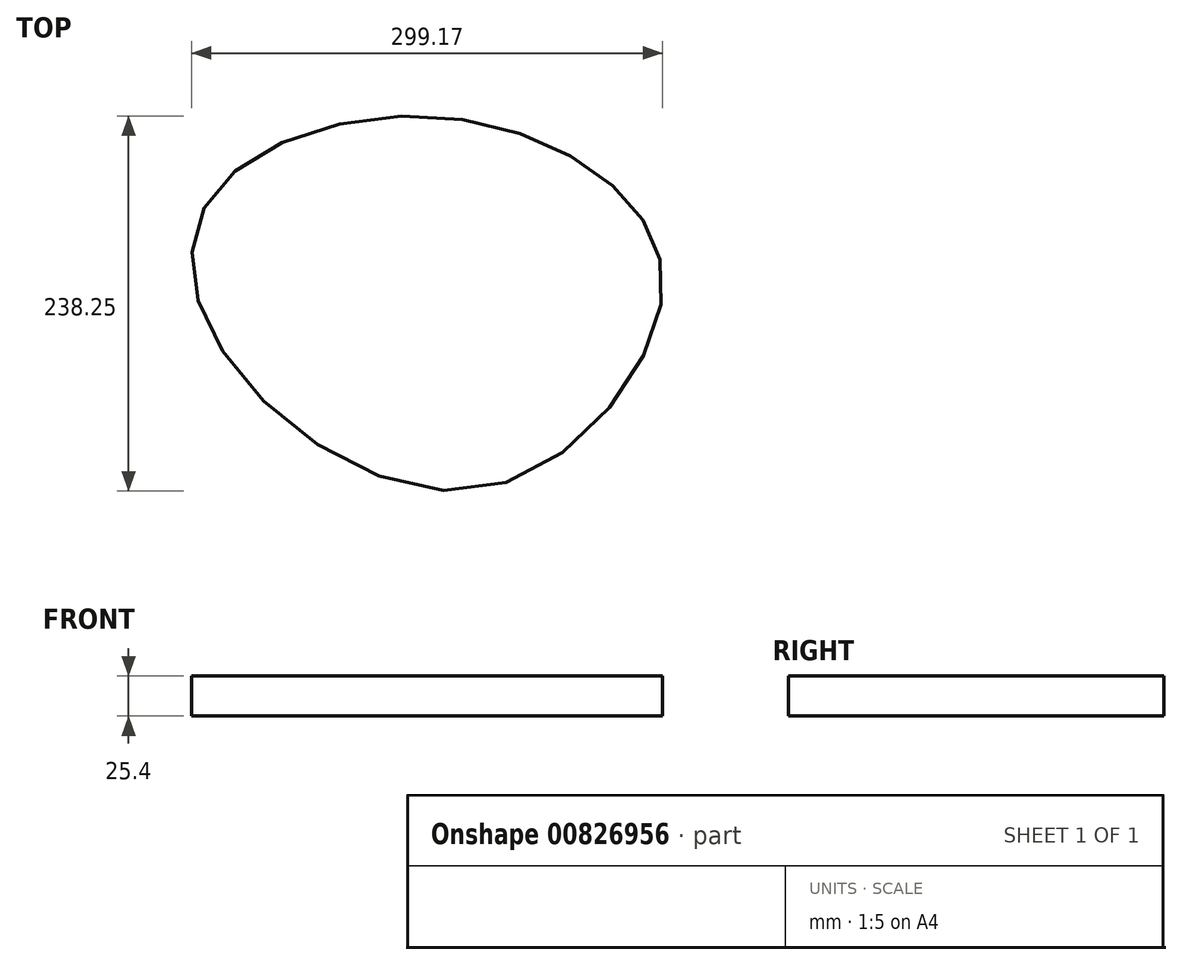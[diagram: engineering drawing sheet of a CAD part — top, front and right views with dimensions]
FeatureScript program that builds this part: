
annotation { "Feature Type Name" : "Feature", "Feature Type Description" : "" }
export const myFeature = defineFeature(function(context is Context, id is Id, definition is map)
    precondition{}
    {
        {
            var Q0;
            Q0=qCreatedBy(makeId("Top.planeOp"),FACE);
            var sketch = newSketch(context, id + "F0", { "sketchPlane" : qUnion([Q0])});
            skFitSpline(sketch, "E0", {"points": [v(-126.11, -21.7) * mm, v(-132.52, 77.96) * mm, v(0, 127.73) * mm, v(126.1, 79.47) * mm, v(150.52, 0) * mm, v(35.67, -109.43) * mm, v(-126.11, -21.7) * mm]});
            skSolve(sketch);
        }
        {
            var Q0;
            Q0=makeQuery(id+"F0.imprint","IMPRINT",FACE,{"disambiguationData":[TD([[makeQuery(id+"F0.imprint","IMPRINT",EDGE,{"derivedFrom":sQuery(id+"F0.wireOp",EDGE,"E0")}),-1.0]])]});
            extrude(context, id + "F1", {"entities" : qUnion([Q0]), "depth" : 25.4 * mm, "offsetDistance" : 25.4 * mm});
        }
    });
